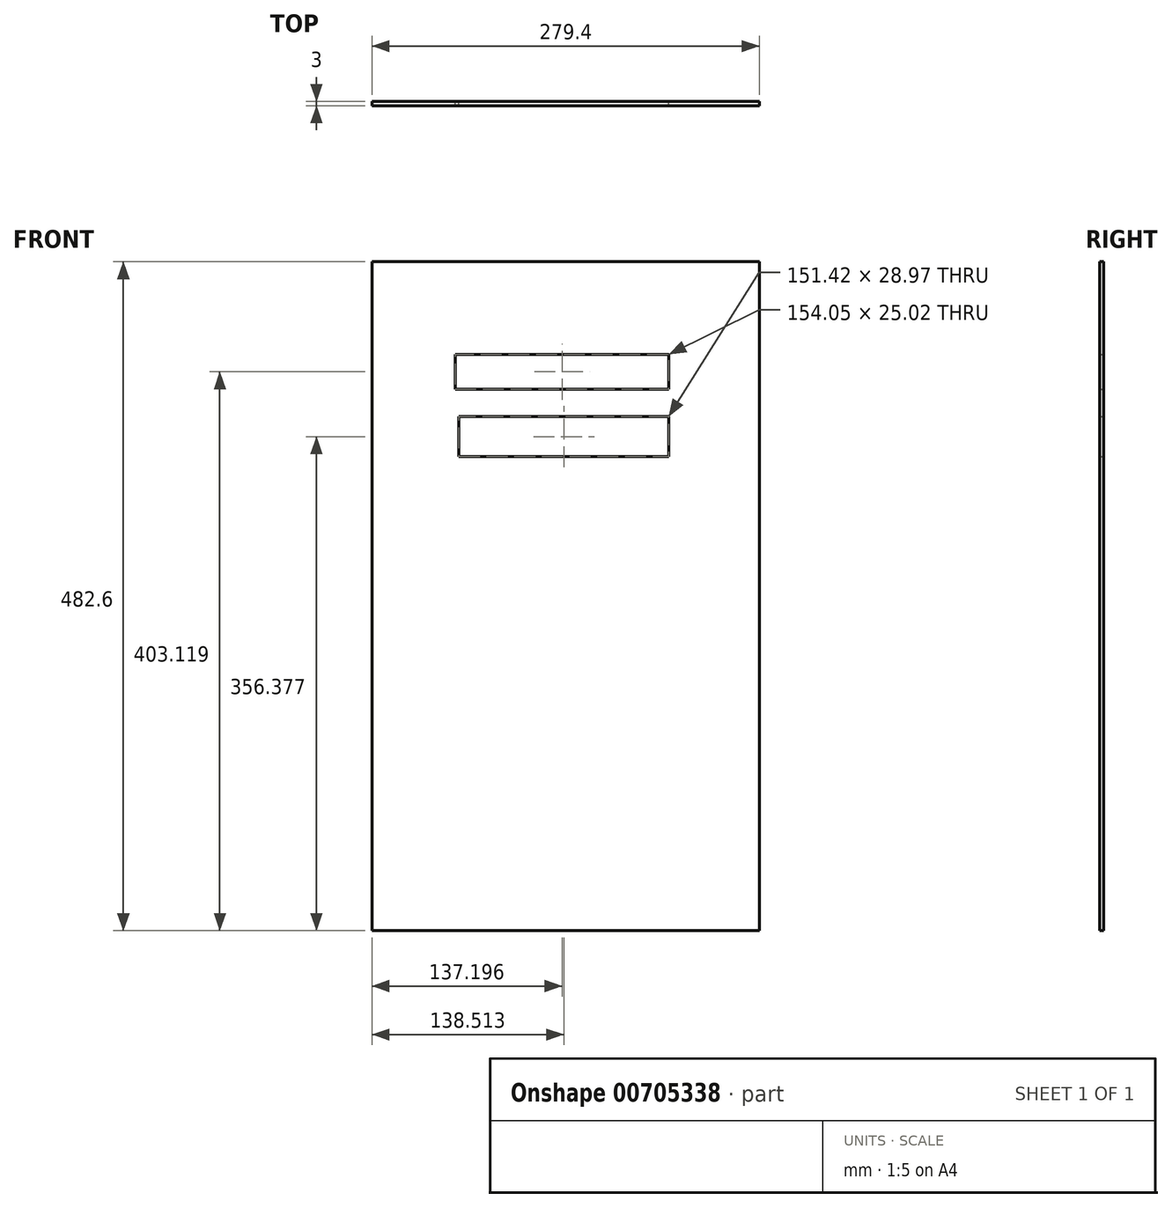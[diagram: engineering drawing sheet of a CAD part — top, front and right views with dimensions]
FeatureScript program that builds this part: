
annotation { "Feature Type Name" : "Feature", "Feature Type Description" : "" }
export const myFeature = defineFeature(function(context is Context, id is Id, definition is map)
    precondition{}
    {
        {
            var Q0;
            Q0=qCreatedBy(makeId("Front.planeOp"),FACE);
            var sketch = newSketch(context, id + "F0", { "sketchPlane" : qUnion([Q0])});
            skLineSegment(sketch, "E0.bottom", {"start": v(-139.7, 241.3) * mm, "end": v(139.7, 241.3) * mm});
            skLineSegment(sketch, "E0.top", {"start": v(-139.7, -241.3) * mm, "end": v(139.7, -241.3) * mm});
            skLineSegment(sketch, "E0.left", {"start": v(-139.7, 241.3) * mm, "end": v(-139.7, -241.3) * mm});
            skLineSegment(sketch, "E0.right", {"start": v(139.7, 241.3) * mm, "end": v(139.7, -241.3) * mm});
            skPoint(sketch, "E0.middle", {"position": v(0, 0) * mm});
            skLineSegment(sketch, "E1.bottom", {"start": v(-79.53, 174.33) * mm, "end": v(74.52, 174.33) * mm});
            skLineSegment(sketch, "E1.top", {"start": v(-79.53, 149.31) * mm, "end": v(74.52, 149.31) * mm});
            skLineSegment(sketch, "E1.left", {"start": v(-79.53, 174.33) * mm, "end": v(-79.53, 149.31) * mm});
            skLineSegment(sketch, "E1.right", {"start": v(74.52, 174.33) * mm, "end": v(74.52, 149.31) * mm});
            skLineSegment(sketch, "E2.bottom", {"start": v(-76.9, 129.56) * mm, "end": v(74.52, 129.56) * mm});
            skLineSegment(sketch, "E2.top", {"start": v(-76.9, 100.6) * mm, "end": v(74.52, 100.6) * mm});
            skLineSegment(sketch, "E2.left", {"start": v(-76.9, 129.56) * mm, "end": v(-76.9, 100.6) * mm});
            skLineSegment(sketch, "E2.right", {"start": v(74.52, 129.56) * mm, "end": v(74.52, 100.6) * mm});
            skSolve(sketch);
        }
        {
            var Q0;
            Q0=makeQuery(id+"F0.imprint","IMPRINT",FACE,{"disambiguationData":[TD([[makeQuery(id+"F0.imprint","IMPRINT",EDGE,{"derivedFrom":sQuery(id+"F0.wireOp",EDGE,"E0.bottom")}),-1.0]])]});
            extrude(context, id + "F1", {"entities" : qUnion([Q0]), "depth" : 3 * mm, "offsetDistance" : 25.4 * mm});
        }
    });
